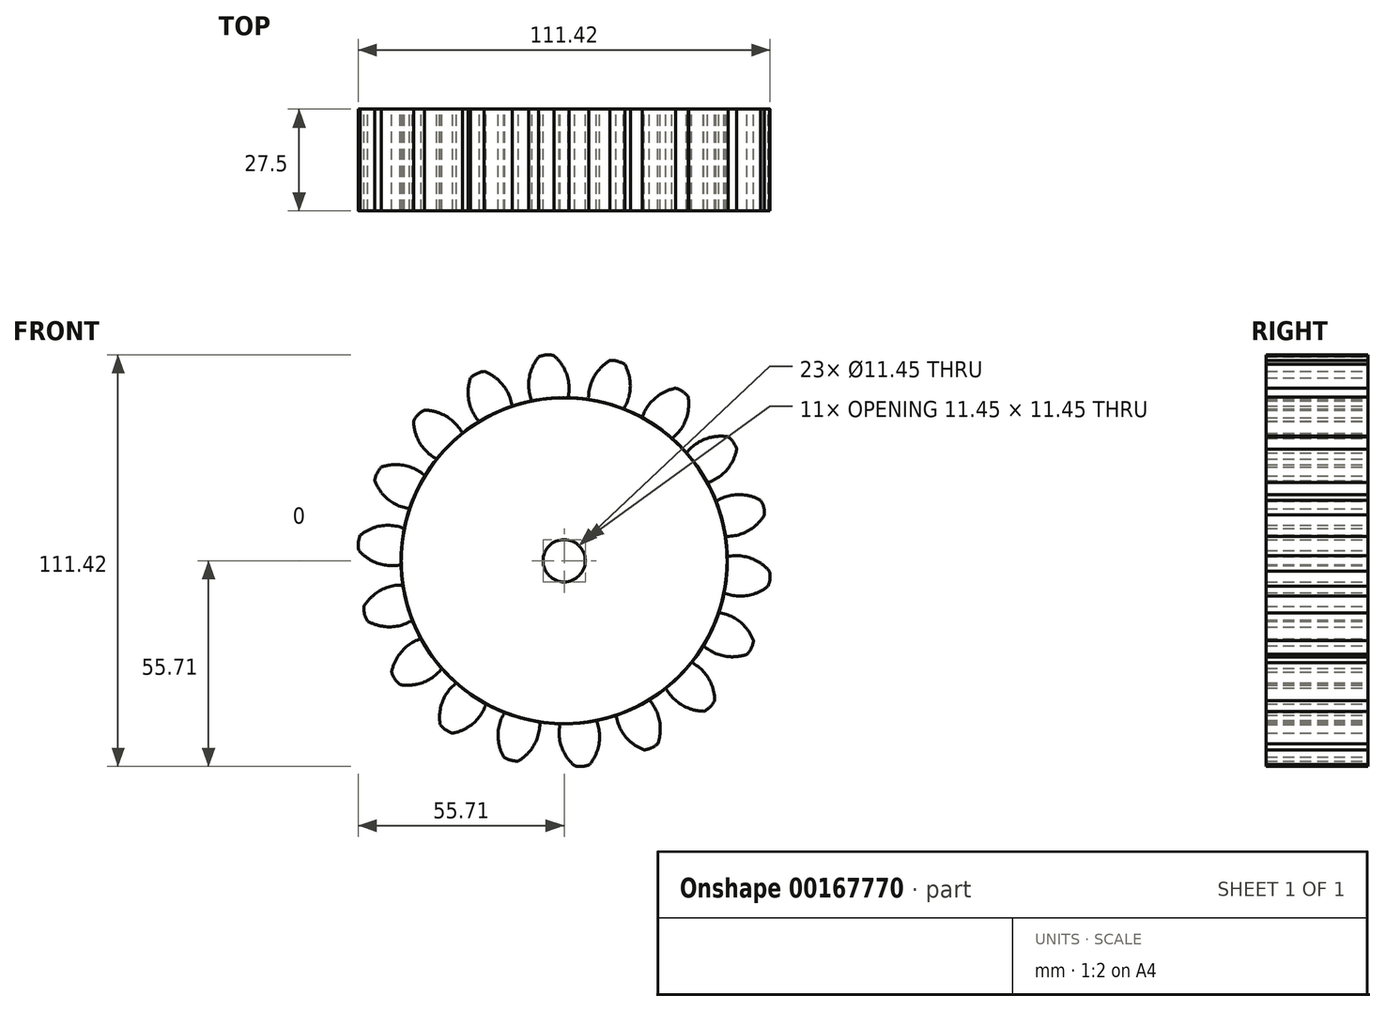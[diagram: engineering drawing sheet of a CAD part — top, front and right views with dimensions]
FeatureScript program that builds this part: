
annotation { "Feature Type Name" : "Feature", "Feature Type Description" : "" }
export const myFeature = defineFeature(function(context is Context, id is Id, definition is map)
    precondition{}
    {
        {
            var Q0;
            Q0=qCreatedBy(makeId("Front.planeOp"),FACE);
            var sketch = newSketch(context, id + "F0", { "sketchPlane" : qUnion([Q0])});
            skCircle(sketch, "E0", {"center": v(0, 0) * mm, "radius": 58.43 * mm, "construction": true});
            skCircle(sketch, "E1", {"center": v(0, 0) * mm, "radius": 52 * mm, "construction": true});
            skCircle(sketch, "E2", {"center": v(0, 0) * mm, "radius": 44.12 * mm});
            skLineSegment(sketch, "E3", {"start": v(0, 0) * mm, "end": v(-6.54, 74.71) * mm});
            skLineSegment(sketch, "E4", {"start": v(-6.54, 74.71) * mm, "end": v(0, 0) * mm, "construction": true});
            skLineSegment(sketch, "E5", {"start": v(0, 0) * mm, "end": v(0, 75) * mm, "construction": true});
            skLineSegment(sketch, "E6", {"start": v(0, 52) * mm, "end": v(-127.38, -3.02) * mm, "construction": true});
            skLineSegment(sketch, "E7", {"start": v(0, 52) * mm, "end": v(-142.61, 43.63) * mm, "construction": true});
            skCircle(sketch, "E8", {"center": v(0, 0) * mm, "radius": 47.74 * mm, "construction": true});
            skCircle(sketch, "E9", {"center": v(0, 52) * mm, "radius": 12 * mm, "construction": true});
            skArc(sketch, "E10", {"start": v(-7.14, 58) * mm, "mid": v(-18.4, 37.34) * mm, "end": v(0, 52) * mm, "construction": true});
            skArc(sketch, "E11", {"start": v(1.07, 44.11) * mm, "mid": v(1.24, 48.15) * mm, "end": v(0, 52) * mm});
            skArc(sketch, "E12", {"start": v(0, 52) * mm, "mid": v(-1.23, 53.9) * mm, "end": v(-2.78, 55.53) * mm});
            skArc(sketch, "E13.MirrorCS", {"start": v(-9.03, 51.21) * mm, "mid": v(-8.14, 53.3) * mm, "end": v(-6.88, 55.19) * mm});
            skArc(sketch, "E14.MirrorCS", {"start": v(-8.72, 43.25) * mm, "mid": v(-9.58, 47.2) * mm, "end": v(-9.03, 51.21) * mm});
            skPoint(sketch, "E15.orphan", {"position": v(-3.04, 58.35) * mm});
            skArc(sketch, "E16", {"start": v(-2.78, 55.53) * mm, "mid": v(-4.86, 55.69) * mm, "end": v(-6.88, 55.19) * mm});
            skArc(sketch, "E17.trimOffspring", {"start": v(-5, 57.07) * mm, "mid": v(-4.98, 57.08) * mm, "end": v(-4.97, 57.09) * mm});
            skArc(sketch, "E18.trimOffspring", {"start": v(-4.97, 57.09) * mm, "mid": v(-4.98, 57.1) * mm, "end": v(-5, 57.1) * mm, "construction": true});
            skSolve(sketch);
        }
        {
            var Q0;
            Q0 = qSketchRegion(id + "F0", true);
            extrude(context, id + "F1", {"entities" : qUnion([Q0]), "depth" : 25 * mm});
        }
        {
            var Q0;
            Q0=makeQuery(id+"F1.opExtrude","CAP_FACE",FACE,{"disambiguationData":[OSD([sQuery(id+"F0.wireOp",EDGE,"E2"),sQuery(id+"F0.wireOp",EDGE,"E11"),sQuery(id+"F0.wireOp",EDGE,"E12"),sQuery(id+"F0.wireOp",EDGE,"E13.MirrorCS"),sQuery(id+"F0.wireOp",EDGE,"E14.MirrorCS"),sQuery(id+"F0.wireOp",EDGE,"E16")])],"isStart":false});
            extrude(context, id + "F2", {"entities" : qUnion([Q0]), "operationType" : NewBodyOperationType.ADD, "endBound" : BoundingType.SYMMETRIC, "depth" : 5 * mm});
        }
        {
            var Q0;
            Q0=makeQuery(id+"F1.opExtrude","SWEPT_BODY",BODY,{"disambiguationData":[OSD([sQuery(id+"F0.wireOp",EDGE,"E2"),sQuery(id+"F0.wireOp",EDGE,"E11"),sQuery(id+"F0.wireOp",EDGE,"E12"),sQuery(id+"F0.wireOp",EDGE,"E13.MirrorCS"),sQuery(id+"F0.wireOp",EDGE,"E14.MirrorCS"),sQuery(id+"F0.wireOp",EDGE,"E16")])]});
            var Q1;
            {var subQ0=sQuery(id+"F0.wireOp",EDGE,"E2");Q1=makeQuery(id+"F2.boolean.opBoolean","MERGE",FACE,{"derivedFrom":[makeQuery(id+"F1.opExtrude","SWEPT_FACE",FACE,{"disambiguationData":[OSD([subQ0])]}),makeQuery(id+"F2.opExtrude","SWEPT_FACE",FACE,{"disambiguationData":[OSD([subQ0])]})]});}
            circularPattern(context, id + "F3", {"entities" : qUnion([Q0]), "axis" : qUnion([Q1]), "angle" : 20 * degree, "instanceCount" : 23});
        }
        {
            var Q0;
            Q0=makeQuery(id+"F1.opExtrude","CAP_FACE",FACE,{"disambiguationData":[OSD([sQuery(id+"F0.wireOp",EDGE,"E2"),sQuery(id+"F0.wireOp",EDGE,"E11"),sQuery(id+"F0.wireOp",EDGE,"E12"),sQuery(id+"F0.wireOp",EDGE,"E13.MirrorCS"),sQuery(id+"F0.wireOp",EDGE,"E14.MirrorCS"),sQuery(id+"F0.wireOp",EDGE,"E16")])],"isStart":true});
            var sketch = newSketch(context, id + "F4", { "sketchPlane" : qUnion([Q0])});
            skCircle(sketch, "E19", {"center": v(0, 0) * mm, "radius": 5.72 * mm});
            skCircle(sketch, "E20", {"center": v(0, 9.27) * mm, "radius": 1.26 * mm});
            skSolve(sketch);
        }
        {
            var Q0;
            Q0=makeQuery(id+"F4.imprint","IMPRINT",FACE,{"disambiguationData":[TD([[makeQuery(id+"F4.imprint","IMPRINT",EDGE,{"derivedFrom":sQuery(id+"F4.wireOp",EDGE,"E19")}),1.0]])]});
            extrude(context, id + "F5", {"entities" : qUnion([Q0]), "operationType" : NewBodyOperationType.REMOVE, "endBound" : BoundingType.THROUGH_ALL, "oppositeDirection" : true, "depth" : 25 * mm});
        }
    });
